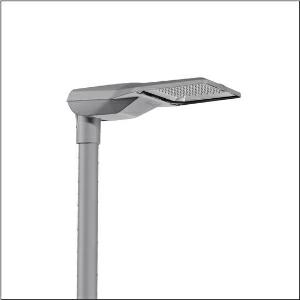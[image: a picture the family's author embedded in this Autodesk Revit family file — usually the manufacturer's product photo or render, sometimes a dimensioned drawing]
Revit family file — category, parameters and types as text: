
# Revit family: streetlight_sl_21_iq_midi___st1_0a_5xe3d41d08nb_8ddf
name_source: partatom
category: Lighting Fixtures
units: mm (PartAtom-declared; Revit-internal decimal feet)

## family parameters
Cut with Voids When Loaded = No
Host = Face
Light Source = No
Part Type = Normal
Room Calculation Point = No
Round Connector Dimension = Use Diameter
Shared = No

## types (1)
- --- (1 x LED, 24250 lm, 155.5 W, 4000K)
    Apparent Load = 155 VA
    CIE Flux Codes = 40 73 97 100 100
    Color Rendering = 70
    Color Temperature = 4000K
    Default Elevation = 1800 mm
    Description = Streetlight SL 21 iQ midi, mast luminaire, primary light control with lens, of PMMA, primary optical cover: cover, of toughened safety glass, transparent, light distribution: ST1.0a, light emission: direct distribution, primary light characteristic: asymmetric, installation type: post-top, side-entry, LED, High Power LED, rated luminous flux: 24.250lm, luminous efficacy: 156lm/W, light colour: 740, colour temperature: 4000K, control: Auto-Match, Temp-Guard, Lumen-Switch, Night-Set, Smart-Wire, Light-Fading, Desk-Remote (wireless, voltage-free reading and setting of iQ features in the workshop via application-optimized NFC function/RFID function), optimised constant luminous flux control (CLO 2.0), pre-setting: linear dimming characteristic, mains connection: 230..240V, AC, 50/60Hz, start of lifetime: 156W, end of service life: 162W, reduction: 69W, luminaire housing, of diecast aluminium, powder-coated, Siteco® metallic grey (DB 702S), corrosivity category C5 mid according to DIN EN ISO 12944, please order mast flange separately, inclination adjustable: 0°, 5°, 10°, 15°, sealing non-destructively replaceable, multi-level sealing system, length: 644mm, width: 335mm, height: 110mm, mast flange for spigot size: 42mm (side-entry): 5XC10008XM4, 60/48mm (side-entry/post-top): 5XC10108XM2, 76/60mm (side-entry/post-top): 5XC10108XM1, protection rating (complete): IP66, insulation class (complete): insulation class II (safety insulation), certification: CE, ENEC, ENEC+, VDE, impact resistance: IK09, permissible operating ambient temperature for outdoor applications: -40..+50°C, standard-compliant lighting for roads and squares, packaging unit: 1 piece

Light Distribution: ST1.0a
    Height = 111 mm
    Lamp = 1 x LED
    Lamp Light Flux = 24250 lm
    Lamp Power = 155.5 W
    Lamp count = 1
    Length = 644 mm
    Luminous efficacy = 156 lm/W
    Manufacturer = Siteco
    ModVariant = No
    Model = 5XE3D41D08NB
    Number of Poles = 1
    OnlyDefault = Yes
    Power Factor = 1
    Product Name = Streetlight SL 21 iQ midi | ST1.0a
    Product group = mast luminaire | pylon top
    ProductGroupID = 6100
    Protection Class = Protection class II
    Protection Degree = IP 66
    RLX_Detail_Level = 1
    RLX_Emergency_Light_Flux = 0 lm
    RLX_Emergency_Type = 0
    RLX_Emergency_Type_DB = No
    RlxData = <blob elided: 90957 chars, md5=f1df8147>
    Socket = socket
    Standby Power = 0 W
    System Light Flux = 24250 lm
    System Power = 155 W
    Type Comments = factory setting: luminous flux: 100 % | dim-lin: 254 | 823 mA
    Type Image = l_1004298.jpg
    URL = http://relux.com
    VarID = @adj_141577
    Voltage = 0 V
    Weight = 0.00 kg
    Width = 336 mm

## geometry (parser evidence)
native form markers: Blend x4, Sweep x12
no freeform markers — native parametric forms only
